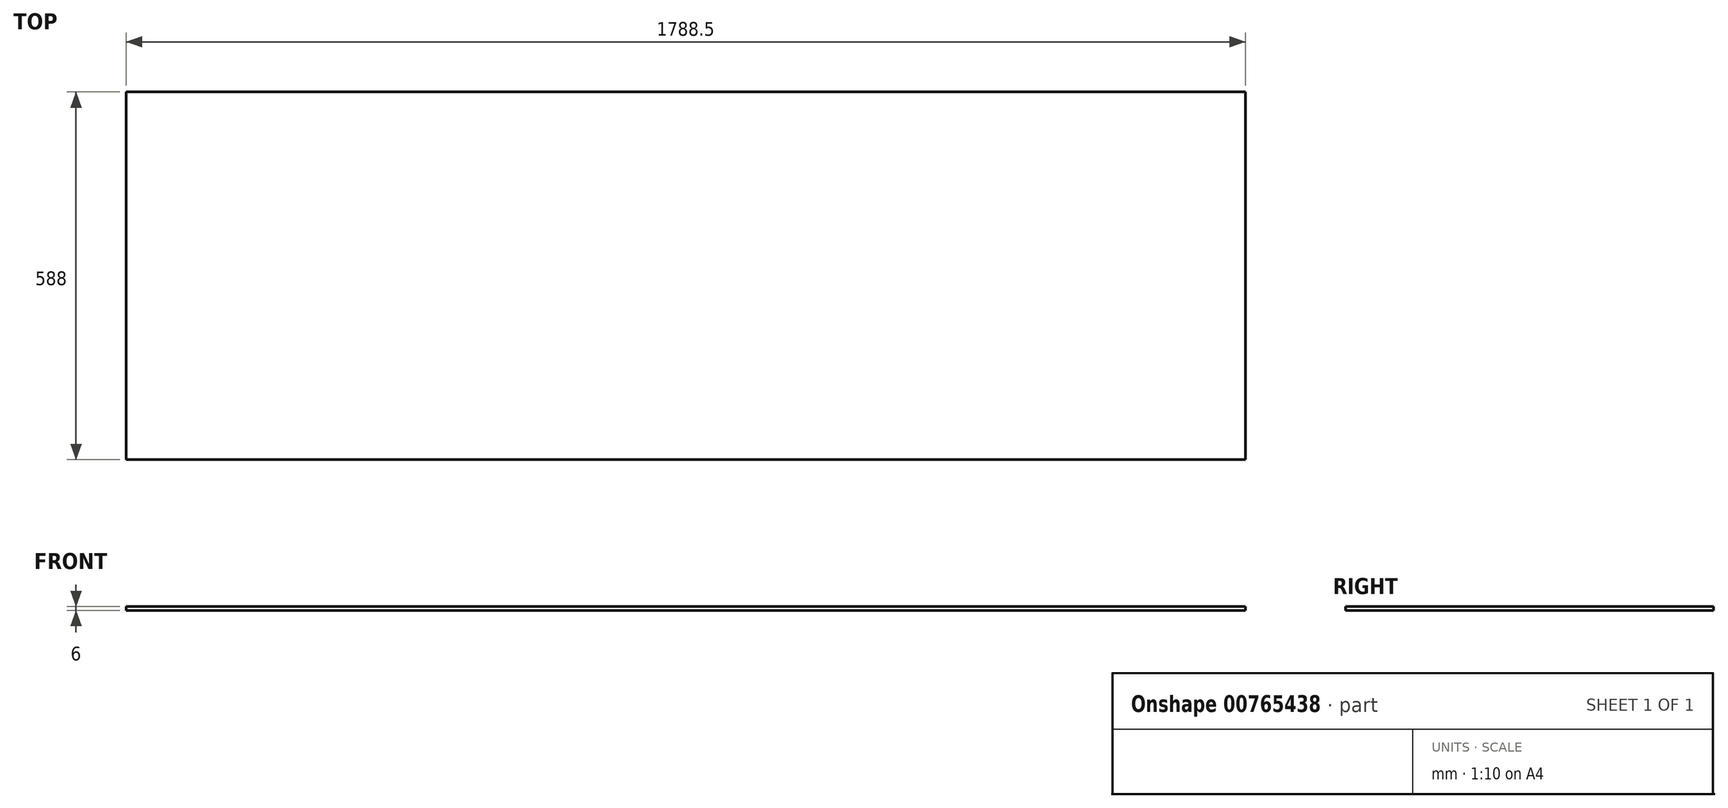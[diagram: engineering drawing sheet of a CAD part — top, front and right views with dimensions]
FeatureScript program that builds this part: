
annotation { "Feature Type Name" : "Feature", "Feature Type Description" : "" }
export const myFeature = defineFeature(function(context is Context, id is Id, definition is map)
    precondition{}
    {
        {
            var Q0;
            Q0=qCreatedBy(makeId("Top.planeOp"),FACE);
            var sketch = newSketch(context, id + "F0", { "sketchPlane" : qUnion([Q0])});
            skLineSegment(sketch, "E0.bottom", {"start": v(-894.25, -294) * mm, "end": v(894.25, -294) * mm});
            skLineSegment(sketch, "E0.top", {"start": v(-894.25, 294) * mm, "end": v(894.25, 294) * mm});
            skLineSegment(sketch, "E0.left", {"start": v(-894.25, -294) * mm, "end": v(-894.25, 294) * mm});
            skLineSegment(sketch, "E0.right", {"start": v(894.25, -294) * mm, "end": v(894.25, 294) * mm});
            skPoint(sketch, "E0.middle", {"position": v(0, 0) * mm});
            skSolve(sketch);
        }
        {
            var Q0;
            Q0 = qSketchRegion(id + "F0", true);
            extrude(context, id + "F1", {"entities" : qUnion([Q0]), "depth" : 6 * mm, "offsetDistance" : 25 * mm});
        }
    });
